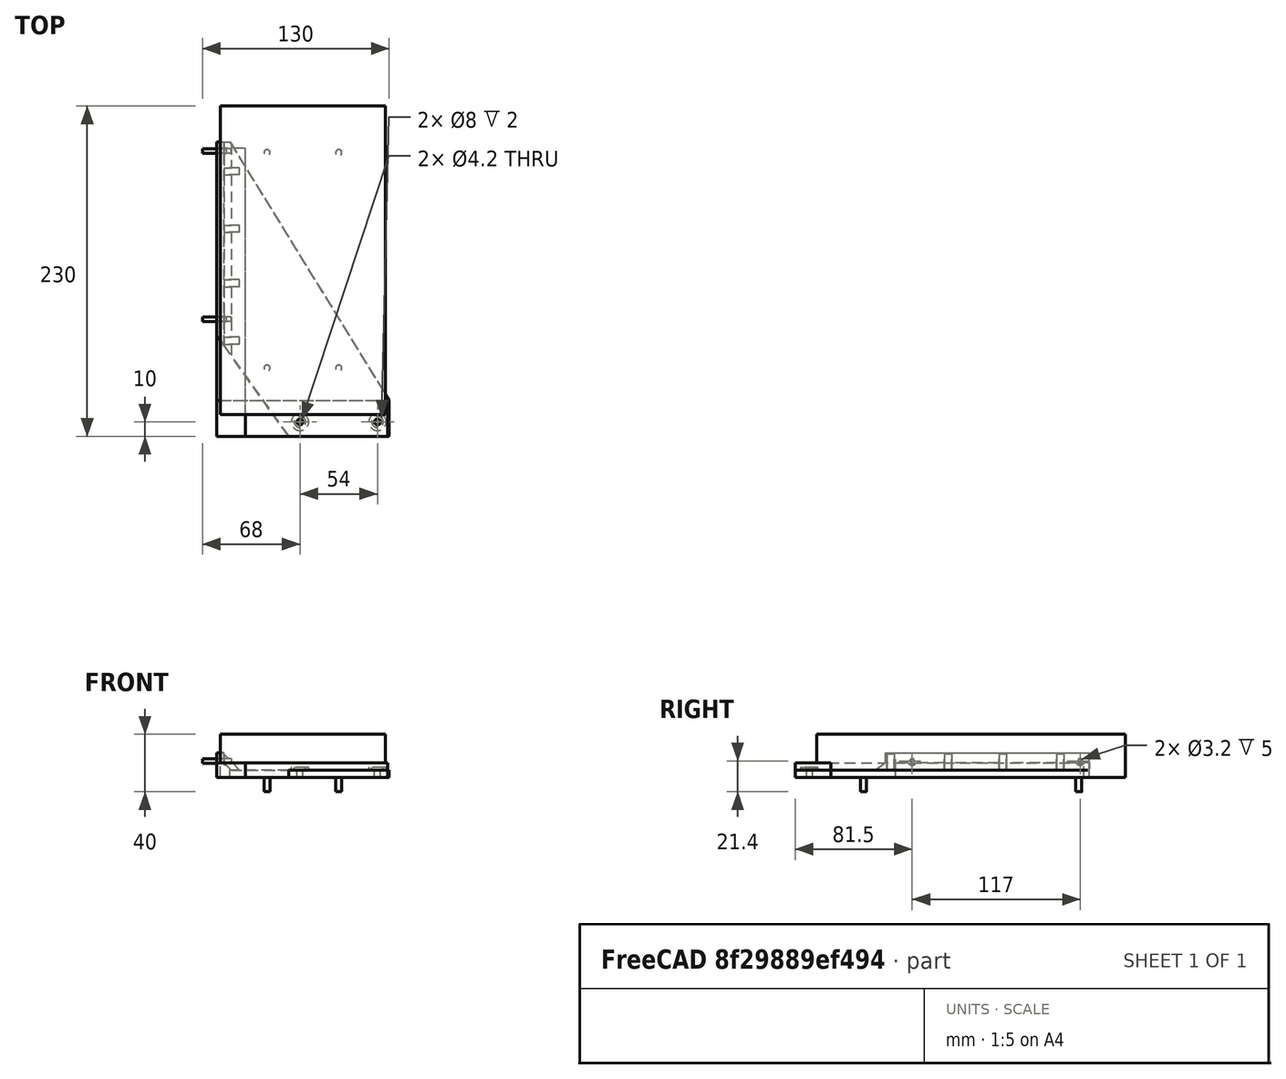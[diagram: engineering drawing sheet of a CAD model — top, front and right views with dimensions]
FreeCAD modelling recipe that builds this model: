
FCSTD DOCUMENT  (FreeCAD 0.18R14555 (Git shallow))
Label: psu-bracket
License: All rights reserved
LicenseURL: http://en.wikipedia.org/wiki/All_rights_reserved
objects: Part::Cylinder×18, Part::MultiFuse×7, Part::Feature×6, Part::Box×5, Part::Cut×4, Part::Chamfer×1
note: 41 computed .brp shape members not serialized (recipe doc carries the construction recipe); baked Part::Feature solids carry a one-line shape summary decoded from their .brp

FEATURE [Part::Cylinder] Cylinder  label="m4-bolt-hole"
  Angle = 360
  AttacherType = Attacher::AttachEngine3D
  Height = 10
  Placement = pos=(112,10,0) rot=(0,0,1;0rad)
  Radius = 2.1
FEATURE [Part::Cylinder] Cylinder001  label="m3-bolt-hole"
  Angle = 360
  AttacherType = Attacher::AttachEngine3D
  Height = 10
  Placement = pos=(5,81.5,11.4) rot=(0,-1,0;1.5708rad)
  Radius = 1.6
FEATURE [Part::Cylinder] Cylinder002  label="m3-bolt-hole001"
  Angle = 360
  AttacherType = Attacher::AttachEngine3D
  Height = 10
  Placement = pos=(5,198.5,11.4) rot=(0,-1,0;1.5708rad)
  Radius = 1.6
FEATURE [Part::Box] Box  label="Cube"
  AttacherType = Attacher::AttachEngine3D
  Height = 17
  Length = 5
  Width = 212
FEATURE [Part::Cylinder] Cylinder003  label="m4-bolt-hole001"
  Angle = 360
  AttacherType = Attacher::AttachEngine3D
  Height = 10
  Placement = pos=(58,10,0) rot=(0,0,1;0rad)
  Radius = 2.1
FEATURE [Part::Feature] Body003  label="Body001"
  shape: bbox 120 x 220 x 5 mm, 6 faces (baked)
FEATURE [Part::MultiFuse] Fusion
  Shapes = -> [Box,Body003]
FEATURE [Part::Chamfer] Chamfer
  Base = -> Fusion
  Edges = 1 edges r=5: [Edge36]
FEATURE [Part::Cylinder] Cylinder004  label="m3-bolt-outer"
  Angle = 360
  AttacherType = Attacher::AttachEngine3D
  Height = 10
  Placement = pos=(15,81.5,11.4) rot=(0,-1,0;1.5708rad)
  Radius = 3
FEATURE [Part::Cylinder] Cylinder005  label="m3-bolt-outer-2"
  Angle = 360
  AttacherType = Attacher::AttachEngine3D
  Height = 10
  Placement = pos=(15,198.5,11.4) rot=(0,-1,0;1.5708rad)
  Radius = 3
FEATURE [Part::MultiFuse] Fusion001
  Shapes = -> [Cylinder004,Cylinder005,Cylinder002,Cylinder001]
FEATURE [Part::Box] Box001  label="Cube001"
  AttacherType = Attacher::AttachEngine3D
  Height = 17
  Length = 15
  Placement = pos=(0,205,0) rot=(0,0,1;0rad)
  Width = 15
FEATURE [Part::Feature] Body004  label="reinforce"
  Placement = pos=(25,147,1) rot=(0,0,1;0rad)
  shape: bbox 15 x 5 x 15 mm, 5 faces (baked)
FEATURE [Part::Cylinder] Cylinder006  label="m4-bolt-outer"
  Angle = 360
  AttacherType = Attacher::AttachEngine3D
  Height = 7
  Placement = pos=(58,10,0) rot=(0,0,1;0rad)
  Radius = 6
FEATURE [Part::Cylinder] Cylinder007  label="m4-bolt-outer-2"
  Angle = 360
  AttacherType = Attacher::AttachEngine3D
  Height = 7
  Placement = pos=(112,10,0) rot=(0,0,1;0rad)
  Radius = 6
FEATURE [Part::Cylinder] Cylinder008  label="m4-bolt-outer001"
  Angle = 360
  AttacherType = Attacher::AttachEngine3D
  Height = 2
  Placement = pos=(58,10,5) rot=(0,0,1;0rad)
  Radius = 4
FEATURE [Part::Cylinder] Cylinder009  label="m4-bolt-outer-003"
  Angle = 360
  AttacherType = Attacher::AttachEngine3D
  Height = 2
  Placement = pos=(112,10,5) rot=(0,0,1;0rad)
  Radius = 4
FEATURE [Part::Feature] Body008  label="Body002"
  Placement = pos=(80,0,0) rot=(0,0,1;0rad)
  shape: bbox 50 x 70 x 20 mm, 5 faces (baked)
FEATURE [Part::Cut] Cut
  Base = -> Chamfer
  Tool = -> Body008
FEATURE [Part::Cut] Cut001
  Base = -> Cut
  Tool = -> Box001
FEATURE [Part::Feature] Body009  label="reinforce001"
  Placement = pos=(25,187,1) rot=(0,0,1;0rad)
  shape: bbox 15 x 5 x 15 mm, 5 faces (baked)
FEATURE [Part::Feature] Body010  label="reinforce002"
  Placement = pos=(25,109,1) rot=(0,0,1;0rad)
  shape: bbox 15 x 5 x 15 mm, 5 faces (baked)
FEATURE [Part::Feature] Body011  label="reinforce003"
  Placement = pos=(25,69,1) rot=(0,0,1;0rad)
  shape: bbox 15 x 5 x 15 mm, 5 faces (baked)
FEATURE [Part::MultiFuse] Fusion002
  Shapes = -> [Body011,Body010,Body009,Body004,Cut001]
FEATURE [Part::Cut] Cut002
  Base = -> Fusion002
  Tool = -> Fusion001
FEATURE [Part::MultiFuse] Fusion003
  Shapes = -> [Cylinder006,Cylinder007,Cut002]
FEATURE [Part::MultiFuse] Fusion004
  Shapes = -> [Cylinder,Cylinder003,Cylinder008,Cylinder009]
FEATURE [Part::Cut] Cut003
  Base = -> Fusion003
  Tool = -> Fusion004
FEATURE [Part::Box] Box002  label="Cube002"
  AttacherType = Attacher::AttachEngine3D
  Height = 10
  Length = 119
  Width = 25
FEATURE [Part::Box] Box003  label="Cube003"
  AttacherType = Attacher::AttachEngine3D
  Height = 10
  Length = 20
  Width = 201
FEATURE [Part::Box] Box004  label="Cube004"
  AttacherType = Attacher::AttachEngine3D
  Height = 30
  Length = 115
  Width = 215
FEATURE [Part::Cylinder] Cylinder010  label="Cylinder"
  Angle = 360
  AttacherType = Attacher::AttachEngine3D
  Height = 40
  Placement = pos=(32.5,32.5,0) rot=(0,0,1;0rad)
  Radius = 2.1
FEATURE [Part::Cylinder] Cylinder011  label="Cylinder001"
  Angle = 360
  AttacherType = Attacher::AttachEngine3D
  Height = 40
  Placement = pos=(32.5,182.5,0) rot=(0,0,1;0rad)
  Radius = 2.1
FEATURE [Part::Cylinder] Cylinder012  label="Cylinder002"
  Angle = 360
  AttacherType = Attacher::AttachEngine3D
  Height = 40
  Placement = pos=(82.5,182.5,0) rot=(0,0,1;0rad)
  Radius = 2.1
FEATURE [Part::Cylinder] Cylinder013  label="Cylinder003"
  Angle = 360
  AttacherType = Attacher::AttachEngine3D
  Height = 40
  Placement = pos=(82.5,32.5,0) rot=(0,0,1;0rad)
  Radius = 2.1
FEATURE [Part::MultiFuse] Fusion005
  Placement = pos=(0,0,-10) rot=(0,0,1;0rad)
  Shapes = -> [Cylinder010,Cylinder011,Cylinder012,Cylinder013]
FEATURE [Part::MultiFuse] Fusion006  label="meanwell-pref"
  Placement = pos=(2.5,15,0) rot=(0,0,1;0rad)
  Shapes = -> [Fusion005,Box004]
FEATURE [Part::Cylinder] Cylinder014  label="bottom-screw-1"
  Angle = 360
  AttacherType = Attacher::AttachEngine3D
  Height = 10
  Placement = pos=(58,10,0) rot=(0,0,1;0rad)
  Radius = 2.1
FEATURE [Part::Cylinder] Cylinder015  label="bottom-screw-2"
  Angle = 360
  AttacherType = Attacher::AttachEngine3D
  Height = 10
  Placement = pos=(112,10,0) rot=(0,0,1;0rad)
  Radius = 2.1
FEATURE [Part::Cylinder] Cylinder016  label="side-screw-1"
  Angle = 360
  AttacherType = Attacher::AttachEngine3D
  Height = 20
  Placement = pos=(10,81.5,11.4) rot=(0,1,0;4.71239rad)
  Radius = 1.6
FEATURE [Part::Cylinder] Cylinder017  label="side-screw-2"
  Angle = 360
  AttacherType = Attacher::AttachEngine3D
  Height = 20
  Placement = pos=(10,198.5,11.4) rot=(0,-1,0;1.5708rad)
  Radius = 1.6
